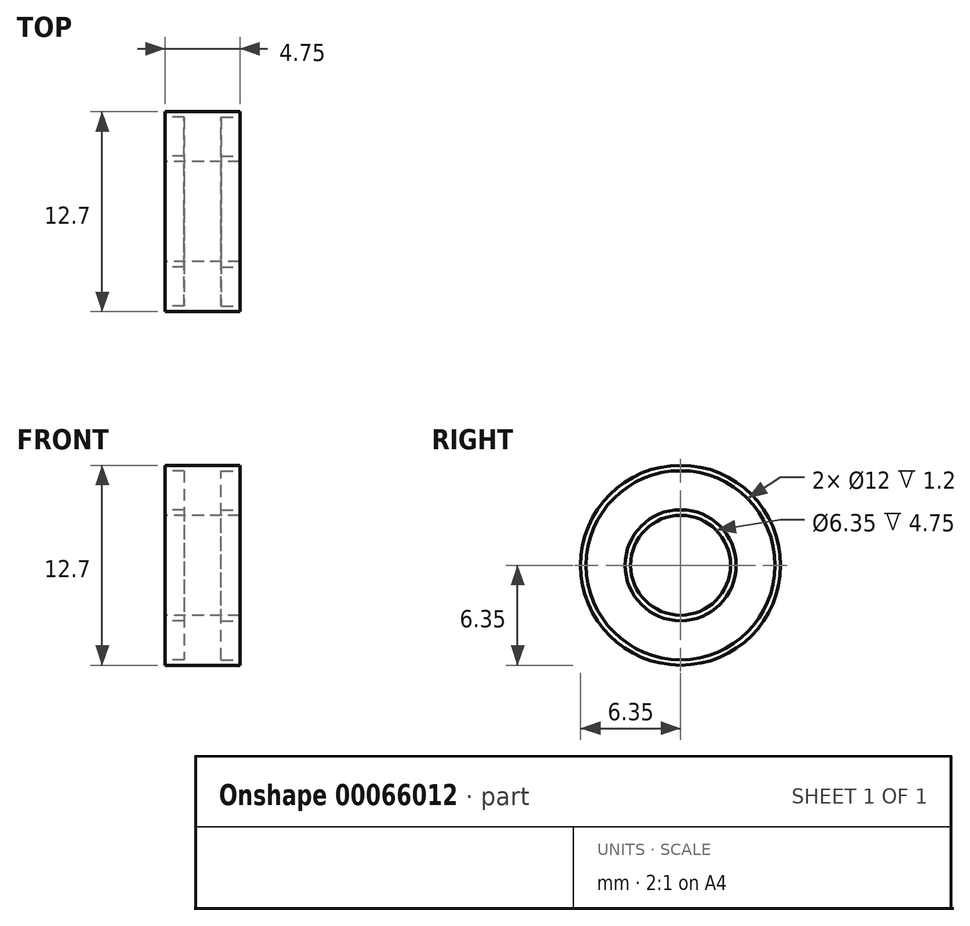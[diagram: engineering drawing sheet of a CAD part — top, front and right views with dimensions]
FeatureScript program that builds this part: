
annotation { "Feature Type Name" : "Feature", "Feature Type Description" : "" }
export const myFeature = defineFeature(function(context is Context, id is Id, definition is map)
    precondition{}
    {
        {
            var Q0;
            Q0=qCreatedBy(makeId("Right.planeOp"),FACE);
            var sketch = newSketch(context, id + "F0", { "sketchPlane" : qUnion([Q0])});
            skCircle(sketch, "E0", {"center": v(0, 0) * mm, "radius": 3.17 * mm});
            skCircle(sketch, "E1", {"center": v(0, 0) * mm, "radius": 6.35 * mm});
            skSolve(sketch);
        }
        {
            var Q0;
            Q0=makeQuery(id+"F0.imprint","IMPRINT",FACE,{"disambiguationData":[TD([[makeQuery(id+"F0.imprint","IMPRINT",EDGE,{"derivedFrom":sQuery(id+"F0.wireOp",EDGE,"E0")}),-1.0]])]});
            extrude(context, id + "F1", {"entities" : qUnion([Q0]), "depth" : 4.75 * mm});
        }
        {
            var Q0;
            Q0=makeQuery(id+"F1.opExtrude","CAP_FACE",FACE,{"disambiguationData":[OSD([sQuery(id+"F0.wireOp",EDGE,"E0"),sQuery(id+"F0.wireOp",EDGE,"E1")])],"isStart":false});
            var sketch = newSketch(context, id + "F2", { "sketchPlane" : qUnion([Q0])});
            skCircle(sketch, "E2", {"center": v(0, 0) * mm, "radius": 3.52 * mm});
            skCircle(sketch, "E3", {"center": v(0, 0) * mm, "radius": 6 * mm});
            skSolve(sketch);
        }
        {
            var Q0;
            Q0=makeQuery(id+"F2.imprint","IMPRINT",FACE,{"disambiguationData":[TD([[makeQuery(id+"F2.imprint","IMPRINT",EDGE,{"derivedFrom":sQuery(id+"F2.wireOp",EDGE,"E2")}),-1.0]])]});
            extrude(context, id + "F3", {"entities" : qUnion([Q0]), "operationType" : NewBodyOperationType.REMOVE, "oppositeDirection" : true, "depth" : 1.2 * mm});
        }
        {
            var Q0;
            Q0=makeQuery(id+"F1.opExtrude","CAP_FACE",FACE,{"disambiguationData":[OSD([sQuery(id+"F0.wireOp",EDGE,"E0"),sQuery(id+"F0.wireOp",EDGE,"E1")])],"isStart":true});
            var sketch = newSketch(context, id + "F4", { "sketchPlane" : qUnion([Q0])});
            skCircle(sketch, "E4", {"center": v(0, 0) * mm, "radius": 3.52 * mm});
            skCircle(sketch, "E5", {"center": v(0, 0) * mm, "radius": 6 * mm});
            skSolve(sketch);
        }
        {
            var Q0;
            Q0 = qSketchRegion(id + "F4", true);
            extrude(context, id + "F5", {"entities" : qUnion([Q0]), "operationType" : NewBodyOperationType.REMOVE, "oppositeDirection" : true, "depth" : 1.2 * mm});
        }
    });
